# Revit family: 712-4820-001-DN40-300
name_source: partatom
category: Pipe Accessories
units: mm (PartAtom-declared; Revit-internal decimal feet)

## family parameters
Always vertical = Yes
Cut with Voids When Loaded = No
Part Type = Valve - Breaks Into
Round Connector Dimension = Use Diameter
Shared = No
Work Plane-Based = No

## types (13) — shared parameters
Body_wallthickness = 10 mm  [stored 0.0328084 ft]
DN040_PN10/16 = 712-0040-48-201
DN050_PN10/16 = 712-0050-48-201
DN065_PN10/16 = 712-0065-48-201
DN080_PN10/16 = 712-0080-48-201
DN100_PN10/16 = 712-0100-48-201
DN125_PN10/16 = 712-0125-48-201
DN150_PN10/16 = 712-0150-48-201
DN200_PN10 = 712-0200-48-200
DN200_PN16 = 712-0200-48-201
DN250_PN10 = 712-0250-48-200
DN250_PN16 = 712-0250-48-201
DN300_PN10 = 712-0300-48-200
DN300_PN16 = 712-0300-48-201
Description_ = AVK FLANGED PIPE W/LOOSE FLANGES
L = 500 mm
Search_Table = 712-4820-001-DN40-300
URL product pages = https://www.avkvalves.com

## per-type parameters (varying)
| type | FOD | Flange_thickness | ID(Radius) | Nominal Diameter (DN) | RF_Thick | Rf_Dia | Rib |
| DN080_PN10/16 | 100 mm  [stored 0.328084 ft] | 19 mm  [stored 0.062336 ft] | 40 mm  [stored 0.131234 ft] | 80 mm  [stored 0.262467 ft] | 3 mm  [stored 0.00984252 ft] | 66 mm  [stored 0.216535 ft] | 20 mm  [stored 0.0656168 ft] |
| DN100_PN10/16 | 110 mm  [stored 0.360892 ft] | 19 mm  [stored 0.062336 ft] | 50 mm  [stored 0.164042 ft] | 100 mm  [stored 0.328084 ft] | 3 mm  [stored 0.00984252 ft] | 78 mm  [stored 0.255906 ft] | 25 mm  [stored 0.082021 ft] |
| DN150_PN10/16 | 143 mm | 20 mm  [stored 0.0656168 ft] | 75 mm | 150 mm  [stored 0.492126 ft] | 4 mm  [stored 0.0131234 ft] | 106 mm | 38 mm |
| DN040_PN10/16 | 75 mm | 19 mm  [stored 0.062336 ft] | 20 mm  [stored 0.0656168 ft] | 40 mm  [stored 0.131234 ft] | 3 mm  [stored 0.00984252 ft] | 42 mm  [stored 0.137795 ft] | 10 mm  [stored 0.0328084 ft] |
| DN050_PN10/16 | 83 mm | 19 mm  [stored 0.062336 ft] | 25 mm  [stored 0.082021 ft] | 50 mm  [stored 0.164042 ft] | 3 mm  [stored 0.00984252 ft] | 50 mm  [stored 0.164042 ft] | 13 mm |
| DN065_PN10/16 | 93 mm  [stored 0.305118 ft] | 19 mm  [stored 0.062336 ft] | 33 mm  [stored 0.108268 ft] | 65 mm  [stored 0.213255 ft] | 3 mm  [stored 0.00984252 ft] | 59 mm | 16 mm |
| DN200_PN10 | 170 mm  [stored 0.557743 ft] | 20 mm  [stored 0.0656168 ft] | 100 mm  [stored 0.328084 ft] | 200 mm  [stored 0.656168 ft] | 4 mm  [stored 0.0131234 ft] | 133 mm  [stored 0.436352 ft] | 50 mm  [stored 0.164042 ft] |
| DN250_PN10 | 200 mm  [stored 0.656168 ft] | 22 mm  [stored 0.0721785 ft] | 125 mm  [stored 0.410105 ft] | 250 mm  [stored 0.82021 ft] | 4 mm  [stored 0.0131234 ft] | 160 mm  [stored 0.524934 ft] | 63 mm  [stored 0.206693 ft] |
| DN250_PN16 | 200 mm  [stored 0.656168 ft] | 22 mm  [stored 0.0721785 ft] | 125 mm  [stored 0.410105 ft] | 250 mm  [stored 0.82021 ft] | 4 mm  [stored 0.0131234 ft] | 160 mm  [stored 0.524934 ft] | 63 mm  [stored 0.206693 ft] |
| DN200_PN16 | 170 mm  [stored 0.557743 ft] | 20 mm  [stored 0.0656168 ft] | 100 mm  [stored 0.328084 ft] | 200 mm  [stored 0.656168 ft] | 4 mm  [stored 0.0131234 ft] | 133 mm  [stored 0.436352 ft] | 50 mm  [stored 0.164042 ft] |
| DN300_PN10 | 228 mm | 24 mm  [stored 0.0787402 ft] | 150 mm  [stored 0.492126 ft] | 300 mm  [stored 0.984252 ft] | 4 mm  [stored 0.0131234 ft] | 185 mm  [stored 0.606955 ft] | 75 mm |
| DN300_PN16 | 228 mm | 24 mm  [stored 0.0787402 ft] | 150 mm  [stored 0.492126 ft] | 300 mm  [stored 0.984252 ft] | 4 mm  [stored 0.0131234 ft] | 185 mm  [stored 0.606955 ft] | 75 mm |
| DN125_PN10/16 | 125 mm  [stored 0.410105 ft] | 19 mm  [stored 0.062336 ft] | 63 mm  [stored 0.206693 ft] | 125 mm  [stored 0.410105 ft] | 3 mm  [stored 0.00984252 ft] | 92 mm  [stored 0.301837 ft] | 31 mm  [stored 0.101706 ft] |

note: [stored X ft] marks values corroborated as IEEE doubles in the binary element streams (Revit-internal decimal feet)

## geometry (parser evidence)
native form markers: Sweep x14
no freeform markers — native parametric forms only
